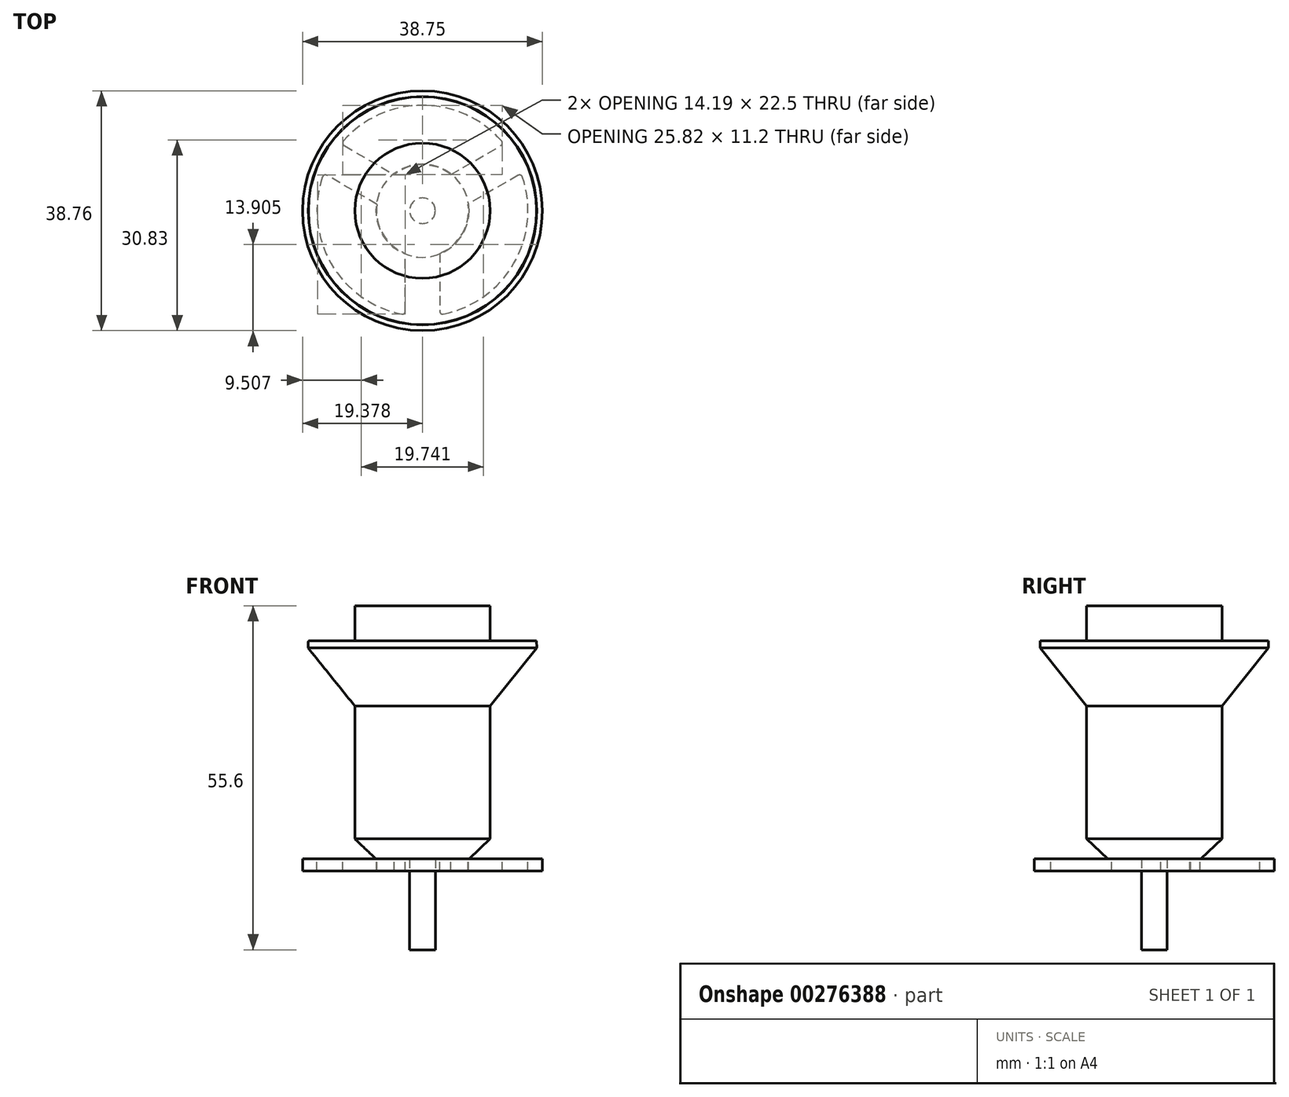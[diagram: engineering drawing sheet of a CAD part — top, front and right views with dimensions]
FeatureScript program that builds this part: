
annotation { "Feature Type Name" : "Feature", "Feature Type Description" : "" }
export const myFeature = defineFeature(function(context is Context, id is Id, definition is map)
    precondition{}
    {
        {
            var Q0;
            Q0=qCreatedBy(makeId("Front.planeOp"),FACE);
            var sketch = newSketch(context, id + "F0", { "sketchPlane" : qUnion([Q0])});
            skLineSegment(sketch, "E0", {"start": v(-6.78, 43.9) * mm, "end": v(-17.7, 43.9) * mm});
            skLineSegment(sketch, "E1", {"start": v(-17.7, 43.9) * mm, "end": v(-17.7, 38.24) * mm});
            skLineSegment(sketch, "E2", {"start": v(-17.7, 38.24) * mm, "end": v(-26.19, 38.24) * mm});
            skLineSegment(sketch, "E3", {"start": v(-26.19, 38.24) * mm, "end": v(-17.7, 27.7) * mm});
            skLineSegment(sketch, "E4", {"start": v(-17.7, 27.7) * mm, "end": v(-17.7, 6.22) * mm});
            skLineSegment(sketch, "E5", {"start": v(-17.7, 6.22) * mm, "end": v(-14.32, 3.01) * mm});
            skLineSegment(sketch, "E6", {"start": v(-14.32, 3.01) * mm, "end": v(-8.85, 3.01) * mm});
            skLineSegment(sketch, "E7", {"start": v(-8.85, 3.01) * mm, "end": v(-8.85, -11.7) * mm});
            skLineSegment(sketch, "E8", {"start": v(-8.85, -11.7) * mm, "end": v(-6.78, -11.7) * mm});
            skLineSegment(sketch, "E9", {"start": v(-6.78, -11.7) * mm, "end": v(-6.78, 43.9) * mm});
            skSolve(sketch);
        }
        {
            var Q0;
            Q0=makeQuery(id+"F0.imprint","IMPRINT",FACE,{"disambiguationData":[TD([[makeQuery(id+"F0.imprint","IMPRINT",EDGE,{"derivedFrom":sQuery(id+"F0.wireOp",EDGE,"E0")}),1.0]])]});
            var Q1;
            Q1=sQuery(id+"F0.wireOp",EDGE,"E9");
            revolve(context, id + "F1", {"entities" : qUnion([Q0]), "axis" : qUnion([Q1]), "revolveType" : RevolveType.FULL});
        }
        {
            var Q0;
            Q0=makeQuery(id+"F1.opRevolve","SWEPT_FACE",FACE,{"disambiguationData":[OSD([sQuery(id+"F0.wireOp",EDGE,"E6")])]});
            var sketch = newSketch(context, id + "F2", { "sketchPlane" : qUnion([Q0])});
            skCircle(sketch, "E10", {"center": v(-6.78, 0) * mm, "radius": 19.38 * mm});
            skArc(sketch, "E11", {"start": v(-10.16, 16.71) * mm, "mid": v(-21.55, 8.53) * mm, "end": v(-22.94, -5.43) * mm});
            skArc(sketch, "E12", {"start": v(-9.56, 6.9) * mm, "mid": v(-13.22, 3.71) * mm, "end": v(-14.14, -1.04) * mm});
            skLineSegment(sketch, "E13", {"start": v(-9.56, 16.22) * mm, "end": v(-9.56, 6.9) * mm});
            skLineSegment(sketch, "E14", {"start": v(-4, 6.9) * mm, "end": v(-4, 16.22) * mm});
            skLineSegment(sketch, "E15.1.0", {"start": v(-19.44, -10.51) * mm, "end": v(-11.36, -5.85) * mm});
            skLineSegment(sketch, "E15.1.3", {"start": v(-14.14, -1.04) * mm, "end": v(-22.22, -5.7) * mm});
            skLineSegment(sketch, "E15.2.0", {"start": v(8.66, -5.7) * mm, "end": v(0.57, -1.04) * mm});
            skLineSegment(sketch, "E15.2.3", {"start": v(-2.2, -5.85) * mm, "end": v(5.88, -10.51) * mm});
            skArc(sketch, "E16.trimOffspring", {"start": v(0.57, -1.04) * mm, "mid": v(-0.35, 3.71) * mm, "end": v(-4, 6.9) * mm});
            skArc(sketch, "E17.trimOffspring", {"start": v(9.38, -5.43) * mm, "mid": v(7.98, 8.53) * mm, "end": v(-3.4, 16.71) * mm});
            skArc(sketch, "E18.trimOffspring", {"start": v(-11.36, -5.85) * mm, "mid": v(-6.78, -7.43) * mm, "end": v(-2.2, -5.85) * mm});
            skArc(sketch, "E19.trimOffspring", {"start": v(-19.57, -11.28) * mm, "mid": v(-6.78, -17.05) * mm, "end": v(6, -11.28) * mm});
            skPoint(sketch, "E20.visualSharp", {"position": v(-9.56, 16.82) * mm});
            skArc(sketch, "E20.filletArc", {"start": v(-9.56, 16.22) * mm, "mid": v(-9.74, 16.61) * mm, "end": v(-10.16, 16.71) * mm});
            skPoint(sketch, "E21.visualSharp", {"position": v(-4, 16.82) * mm});
            skArc(sketch, "E21.filletArc", {"start": v(-3.4, 16.71) * mm, "mid": v(-3.82, 16.61) * mm, "end": v(-4, 16.22) * mm});
            skPoint(sketch, "E22.visualSharp", {"position": v(9.17, -6) * mm});
            skArc(sketch, "E22.filletArc", {"start": v(8.66, -5.7) * mm, "mid": v(9.08, -5.74) * mm, "end": v(9.38, -5.43) * mm});
            skPoint(sketch, "E23.visualSharp", {"position": v(-22.74, -6) * mm});
            skArc(sketch, "E23.filletArc", {"start": v(-22.94, -5.43) * mm, "mid": v(-22.65, -5.74) * mm, "end": v(-22.22, -5.7) * mm});
            skPoint(sketch, "E24.visualSharp", {"position": v(-19.96, -10.81) * mm});
            skArc(sketch, "E24.filletArc", {"start": v(-19.44, -10.51) * mm, "mid": v(-19.69, -10.87) * mm, "end": v(-19.57, -11.28) * mm});
            skPoint(sketch, "E25.visualSharp", {"position": v(6.4, -10.81) * mm});
            skArc(sketch, "E25.filletArc", {"start": v(6, -11.28) * mm, "mid": v(6.12, -10.87) * mm, "end": v(5.88, -10.51) * mm});
            skSolve(sketch);
        }
        {
            var Q0;
            Q0 = qSketchRegion(id + "F2", true);
            extrude(context, id + "F3", {"entities" : qUnion([Q0]), "depth" : 2 * mm});
        }
        {
            var Q0;
            Q0=makeQuery(id+"F1.opRevolve","SWEPT_EDGE",EDGE,{"disambiguationData":[OSD([sQuery(id+"F0.wireOp",EDGE,"E2"),sQuery(id+"F0.wireOp",EDGE,"E3")])]});
            chamfer(context, id + "F4", {"entities" : qUnion([Q0]), "chamferType" : ChamferType.OFFSET_ANGLE, "width" : 1.5 * mm, "oppositeDirection" : false, "angle" : 40 * degree});
        }
    });
